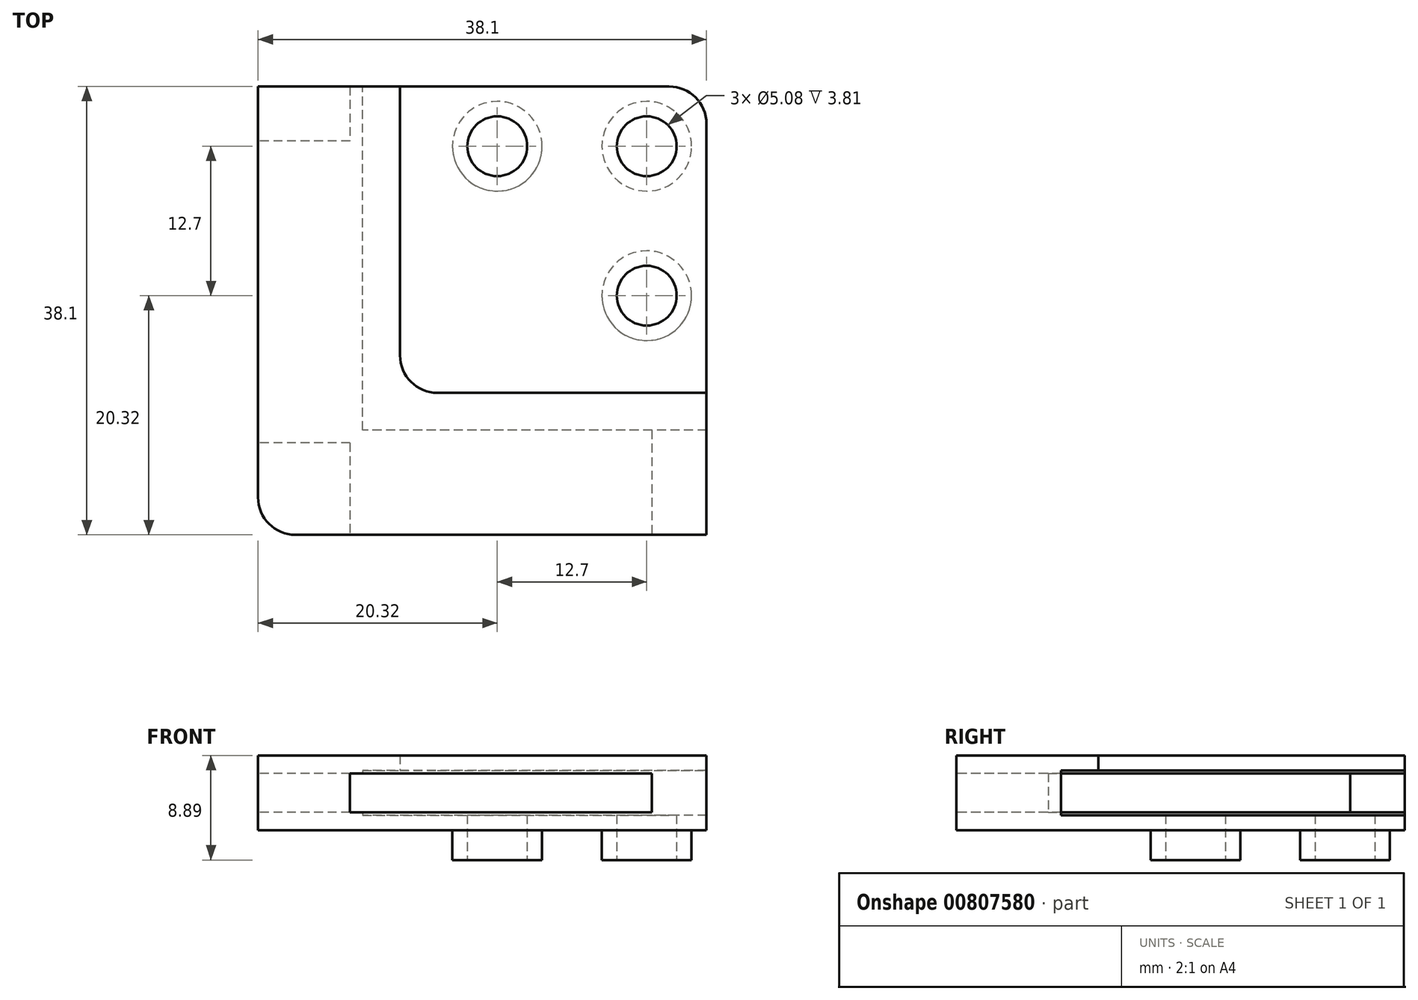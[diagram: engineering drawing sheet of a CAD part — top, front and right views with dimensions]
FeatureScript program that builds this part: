
annotation { "Feature Type Name" : "Feature", "Feature Type Description" : "" }
export const myFeature = defineFeature(function(context is Context, id is Id, definition is map)
    precondition{}
    {
        {
            var Q0;
            Q0=qCreatedBy(makeId("Top.planeOp"),FACE);
            var sketch = newSketch(context, id + "F0", { "sketchPlane" : qUnion([Q0])});
            skLineSegment(sketch, "E0", {"start": v(0, 3.18) * mm, "end": v(0, 38.1) * mm});
            skLineSegment(sketch, "E1", {"start": v(0, 38.1) * mm, "end": v(34.92, 38.1) * mm});
            skLineSegment(sketch, "E2", {"start": v(38.1, 34.93) * mm, "end": v(38.1, 0) * mm});
            skLineSegment(sketch, "E3", {"start": v(38.1, 0) * mm, "end": v(3.18, 0) * mm});
            skPoint(sketch, "E4.visualSharp", {"position": v(0, 0) * mm});
            skArc(sketch, "E4.filletArc", {"start": v(0, 3.18) * mm, "mid": v(0.93, 0.93) * mm, "end": v(3.18, 0) * mm});
            skPoint(sketch, "E5.visualSharp", {"position": v(38.1, 38.1) * mm});
            skArc(sketch, "E5.filletArc", {"start": v(38.1, 34.93) * mm, "mid": v(37.17, 37.17) * mm, "end": v(34.92, 38.1) * mm});
            skSolve(sketch);
        }
        {
            var Q0;
            Q0=makeQuery(id+"F0.imprint","IMPRINT",FACE,{"disambiguationData":[TD([[makeQuery(id+"F0.imprint","IMPRINT",EDGE,{"derivedFrom":sQuery(id+"F0.wireOp",EDGE,"E0")}),-1.0]])]});
            extrude(context, id + "F1", {"entities" : qUnion([Q0]), "depth" : 1.27 * mm, "offsetDistance" : 25.4 * mm});
        }
        {
            var Q0;
            Q0=makeQuery(id+"F1.opExtrude","CAP_FACE",FACE,{"disambiguationData":[OSD([sQuery(id+"F0.wireOp",EDGE,"E0"),sQuery(id+"F0.wireOp",EDGE,"E1"),sQuery(id+"F0.wireOp",EDGE,"1fo0Aqs2-ToZF-Awpb-O64W-LK4OHHaAkrWZ"),sQuery(id+"F0.wireOp",EDGE,"ecCzNfj9-o1Kk-8U93-9Pon-MlgbN1gIHaCP"),sQuery(id+"F0.wireOp",EDGE,"E2"),sQuery(id+"F0.wireOp",EDGE,"E3"),sQuery(id+"F0.wireOp",EDGE,"3e42690f-efb2-42f1-844e-d3d4241bcfd3.filletArc"),sQuery(id+"F0.wireOp",EDGE,"E4.filletArc")])],"isStart":false});
            var sketch = newSketch(context, id + "F2", { "sketchPlane" : qUnion([Q0])});
            skLineSegment(sketch, "E6.0", {"start": v(0, 3.18) * mm, "end": v(0, 38.1) * mm});
            skArc(sketch, "E6.1", {"start": v(0, 3.18) * mm, "mid": v(0.93, 0.93) * mm, "end": v(3.18, 0) * mm});
            skLineSegment(sketch, "E6.2", {"start": v(38.1, 0) * mm, "end": v(3.18, 0) * mm});
            skLineSegment(sketch, "E7.0", {"start": v(8.9, 8.9) * mm, "end": v(8.9, 38.1) * mm});
            skLineSegment(sketch, "E7.1", {"start": v(38.1, 8.9) * mm, "end": v(8.9, 8.9) * mm});
            skLineSegment(sketch, "E8", {"start": v(0, 38.1) * mm, "end": v(8.9, 38.1) * mm});
            skLineSegment(sketch, "E9", {"start": v(38.1, 0) * mm, "end": v(38.1, 8.9) * mm});
            skSolve(sketch);
        }
        {
            var Q0;
            Q0 = qSketchRegion(id + "F2", true);
            extrude(context, id + "F3", {"entities" : qUnion([Q0]), "operationType" : NewBodyOperationType.ADD, "depth" : 3.8 * mm, "offsetDistance" : 25.4 * mm});
        }
        {
            var Q0;
            Q0=makeQuery(id+"F3.opExtrude","CAP_FACE",FACE,{"disambiguationData":[OSD([sQuery(id+"F2.wireOp",EDGE,"E6.0"),sQuery(id+"F2.wireOp",EDGE,"E6.1"),sQuery(id+"F2.wireOp",EDGE,"E6.2"),sQuery(id+"F2.wireOp",EDGE,"E7.0"),sQuery(id+"F2.wireOp",EDGE,"E7.1"),sQuery(id+"F2.wireOp",EDGE,"E8"),sQuery(id+"F2.wireOp",EDGE,"E9")])],"isStart":false});
            var sketch = newSketch(context, id + "F4", { "sketchPlane" : qUnion([Q0])});
            skLineSegment(sketch, "E10.0", {"start": v(8.9, 38.1) * mm, "end": v(12.06, 38.1) * mm});
            skLineSegment(sketch, "E10.1", {"start": v(0, 3.18) * mm, "end": v(0, 38.1) * mm});
            skArc(sketch, "E10.2", {"start": v(0, 3.18) * mm, "mid": v(0.93, 0.93) * mm, "end": v(3.18, 0) * mm});
            skLineSegment(sketch, "E10.3", {"start": v(38.1, 0) * mm, "end": v(3.18, 0) * mm});
            skLineSegment(sketch, "E10.4", {"start": v(38.1, 12.06) * mm, "end": v(38.1, 8.9) * mm});
            skLineSegment(sketch, "E10.5", {"start": v(38.1, 8.9) * mm, "end": v(38.1, 0) * mm});
            skLineSegment(sketch, "E10.6", {"start": v(15.24, 12.06) * mm, "end": v(38.1, 12.06) * mm});
            skArc(sketch, "E10.7", {"start": v(12.07, 15.24) * mm, "mid": v(13, 13) * mm, "end": v(15.24, 12.06) * mm});
            skLineSegment(sketch, "E10.8", {"start": v(12.06, 38.1) * mm, "end": v(12.07, 15.24) * mm});
            skLineSegment(sketch, "E11.0", {"start": v(0, 38.1) * mm, "end": v(8.9, 38.1) * mm});
            skSolve(sketch);
        }
        {
            var Q0;
            Q0 = qSketchRegion(id + "F4", true);
            extrude(context, id + "F5", {"entities" : qUnion([Q0]), "operationType" : NewBodyOperationType.ADD, "depth" : 1.27 * mm, "offsetDistance" : 25.4 * mm});
        }
        {
            var Q0;
            Q0=makeQuery(id+"F5.boolean.opBoolean","MERGE",FACE,{"derivedFrom":[makeQuery(id+"F3.boolean.opBoolean","MERGE",FACE,{"derivedFrom":[makeQuery(id+"F1.opExtrude","SWEPT_FACE",FACE,{"disambiguationData":[OSD([sQuery(id+"F0.wireOp",EDGE,"E3")])]}),makeQuery(id+"F3.opExtrude","SWEPT_FACE",FACE,{"disambiguationData":[OSD([sQuery(id+"F2.wireOp",EDGE,"E6.2")])]})]}),makeQuery(id+"F5.opExtrude","SWEPT_FACE",FACE,{"disambiguationData":[OSD([sQuery(id+"F4.wireOp",EDGE,"E10.3")])]})]});
            var sketch = newSketch(context, id + "F6", { "sketchPlane" : qUnion([Q0])});
            skLineSegment(sketch, "E12.bottom", {"start": v(33.46, 4.83) * mm, "end": v(7.81, 4.83) * mm});
            skLineSegment(sketch, "E12.top", {"start": v(33.46, 1.52) * mm, "end": v(7.81, 1.52) * mm});
            skLineSegment(sketch, "E12.left", {"start": v(33.46, 4.83) * mm, "end": v(33.46, 1.52) * mm});
            skLineSegment(sketch, "E12.right", {"start": v(7.81, 4.83) * mm, "end": v(7.81, 1.52) * mm});
            skPoint(sketch, "E12.middle", {"position": v(20.64, 3.18) * mm});
            skPoint(sketch, "E12.middle.positionSnap0", {"position": v(20.64, 6.35) * mm});
            skPoint(sketch, "E12.middle.positionSnap1", {"position": v(38.1, 3.18) * mm});
            skPoint(sketch, "E12.centerSnap0", {"position": v(20.64, 6.35) * mm});
            skPoint(sketch, "E12.centerSnap1", {"position": v(38.1, 3.18) * mm});
            skSolve(sketch);
        }
        {
            var Q0;
            Q0 = qSketchRegion(id + "F6", true);
            extrude(context, id + "F7", {"entities" : qUnion([Q0]), "operationType" : NewBodyOperationType.REMOVE, "endBound" : BoundingType.THROUGH_ALL, "oppositeDirection" : true, "depth" : 25.4 * mm, "offsetDistance" : 25.4 * mm});
        }
        {
            var Q0;
            Q0=makeQuery(id+"F5.boolean.opBoolean","MERGE",FACE,{"derivedFrom":[makeQuery(id+"F3.boolean.opBoolean","MERGE",FACE,{"derivedFrom":[makeQuery(id+"F1.opExtrude","SWEPT_FACE",FACE,{"disambiguationData":[OSD([sQuery(id+"F0.wireOp",EDGE,"E0")])]}),makeQuery(id+"F3.opExtrude","SWEPT_FACE",FACE,{"disambiguationData":[OSD([sQuery(id+"F2.wireOp",EDGE,"E6.0")])]})]}),makeQuery(id+"F5.opExtrude","SWEPT_FACE",FACE,{"disambiguationData":[OSD([sQuery(id+"F4.wireOp",EDGE,"E10.1")])]})]});
            var sketch = newSketch(context, id + "F8", { "sketchPlane" : qUnion([Q0])});
            skLineSegment(sketch, "E13.bottom", {"start": v(-7.81, 4.83) * mm, "end": v(-33.46, 4.83) * mm});
            skLineSegment(sketch, "E13.top", {"start": v(-7.81, 1.52) * mm, "end": v(-33.46, 1.52) * mm});
            skLineSegment(sketch, "E13.left", {"start": v(-7.81, 4.83) * mm, "end": v(-7.81, 1.52) * mm});
            skLineSegment(sketch, "E13.right", {"start": v(-33.46, 4.83) * mm, "end": v(-33.46, 1.52) * mm});
            skPoint(sketch, "E13.middle", {"position": v(-20.64, 3.18) * mm});
            skPoint(sketch, "E13.middle.positionSnap0", {"position": v(-20.64, 6.35) * mm});
            skPoint(sketch, "E13.middle.positionSnap1", {"position": v(-38.1, 3.18) * mm});
            skPoint(sketch, "E13.centerSnap0", {"position": v(-20.64, 6.35) * mm});
            skPoint(sketch, "E13.centerSnap1", {"position": v(-38.1, 3.18) * mm});
            skSolve(sketch);
        }
        {
            var Q0;
            Q0 = qSketchRegion(id + "F8", true);
            extrude(context, id + "F9", {"entities" : qUnion([Q0]), "operationType" : NewBodyOperationType.REMOVE, "oppositeDirection" : true, "depth" : 25.4 * mm, "offsetDistance" : 25.4 * mm});
        }
        {
            var Q0;
            Q0=makeQuery(id+"F1.opExtrude","CAP_FACE",FACE,{"disambiguationData":[OSD([sQuery(id+"F0.wireOp",EDGE,"E0"),sQuery(id+"F0.wireOp",EDGE,"E1"),sQuery(id+"F0.wireOp",EDGE,"E2"),sQuery(id+"F0.wireOp",EDGE,"E3"),sQuery(id+"F0.wireOp",EDGE,"E4.filletArc"),sQuery(id+"F0.wireOp",EDGE,"E5.filletArc")])],"isStart":true});
            var sketch = newSketch(context, id + "F10", { "sketchPlane" : qUnion([Q0])});
            skCircle(sketch, "E14", {"center": v(33.02, -33.02) * mm, "radius": 3.81 * mm});
            skCircle(sketch, "E15", {"center": v(33.02, -20.32) * mm, "radius": 3.81 * mm});
            skCircle(sketch, "E16", {"center": v(20.32, -33.02) * mm, "radius": 3.81 * mm});
            skSolve(sketch);
        }
        {
            var Q0;
            Q0 = qSketchRegion(id + "F10", true);
            extrude(context, id + "F11", {"entities" : qUnion([Q0]), "operationType" : NewBodyOperationType.ADD, "depth" : 2.54 * mm, "offsetDistance" : 25.4 * mm});
        }
        {
            var Q0;
            Q0=makeQuery(id+"F11.opExtrude","CAP_FACE",FACE,{"disambiguationData":[OSD([sQuery(id+"F10.wireOp",EDGE,"E16")])],"isStart":false});
            var sketch = newSketch(context, id + "F12", { "sketchPlane" : qUnion([Q0])});
            skPoint(sketch, "E17", {"position": v(20.32, -33.02) * mm});
            skCircle(sketch, "E18.0", {"center": v(33.02, -33.02) * mm, "radius": 3.8 * mm, "construction": true});
            skCircle(sketch, "E18.1", {"center": v(33.02, -20.32) * mm, "radius": 3.81 * mm, "construction": true});
            skSolve(sketch);
        }
        {
            var Q0;
            Q0=sQuery(id+"F12.wireOp",VERTEX,"E17");
            var Q1;
            Q1=sQuery(id+"F12.wireOp",VERTEX,"E18.0.center");
            var Q2;
            Q2=sQuery(id+"F12.wireOp",VERTEX,"E18.1.center");
            var Q3;
            Q3=makeQuery(id+"F1.opExtrude","SWEPT_BODY",BODY,{"disambiguationData":[OSD([sQuery(id+"F0.wireOp",EDGE,"E0"),sQuery(id+"F0.wireOp",EDGE,"E1"),sQuery(id+"F0.wireOp",EDGE,"E2"),sQuery(id+"F0.wireOp",EDGE,"E3"),sQuery(id+"F0.wireOp",EDGE,"E4.filletArc"),sQuery(id+"F0.wireOp",EDGE,"E5.filletArc")])]});
            hole(context, id + "F13", {"style" : HoleStyle.SIMPLE, "endStyle" : HoleEndStyle.THROUGH, "holeDiameter" : 5.08 * mm, "majorDiameter" : 6.35 * mm, "isTappedThrough" : true, "tappedDepth" : 3.17 * mm, "tapClearance" : 3, "startFromSketch" : true, "locations" : qUnion([Q0, Q1, Q2]), "scope" : qUnion([Q3])});
        }
    });
